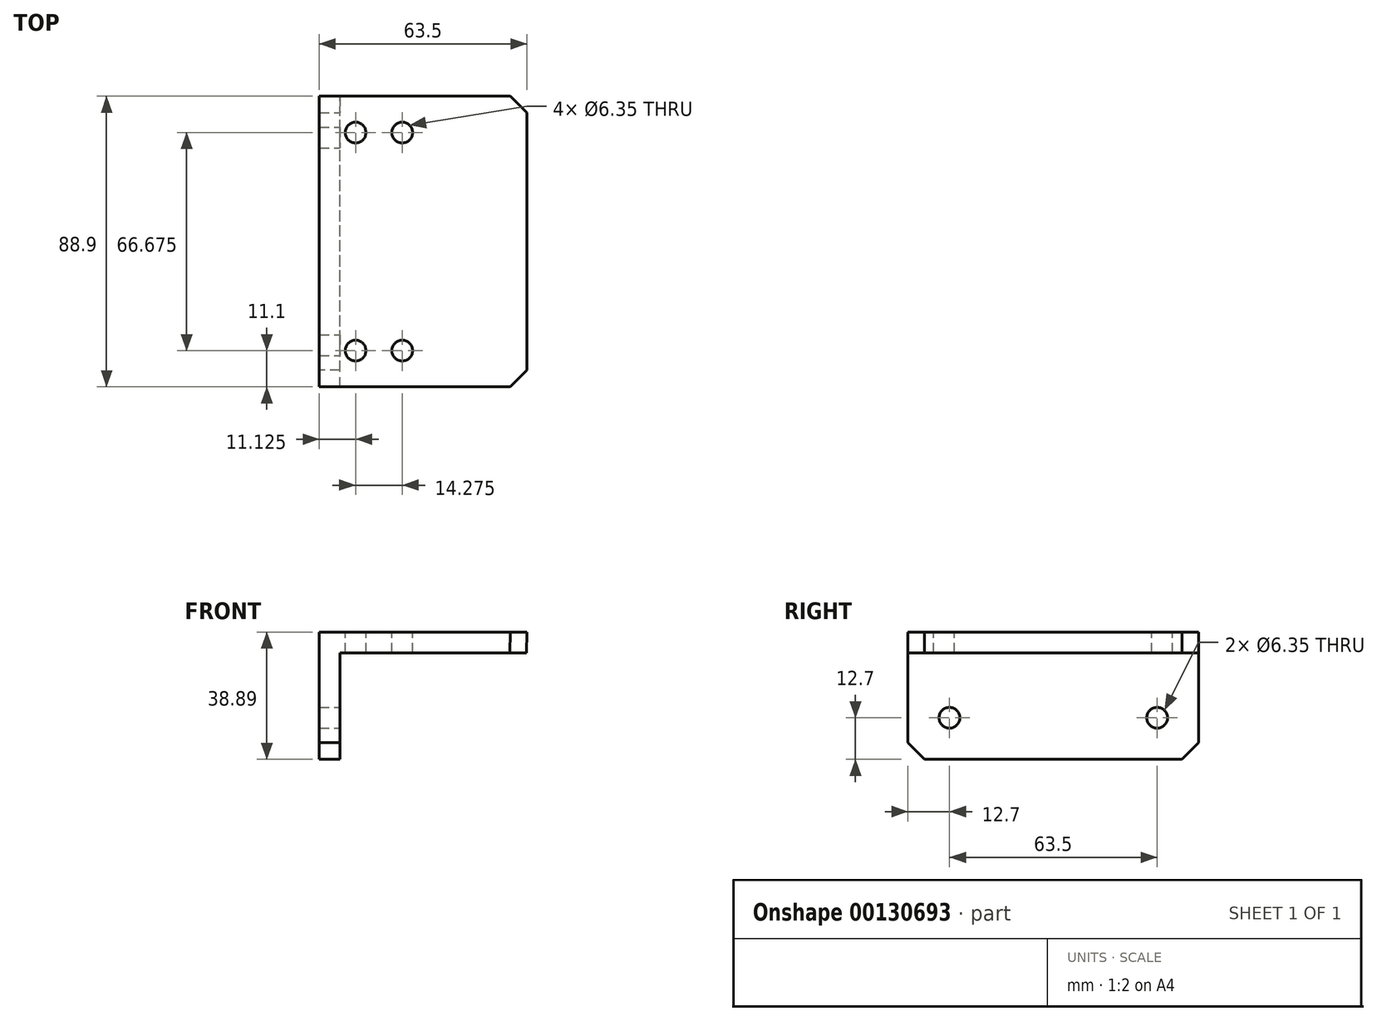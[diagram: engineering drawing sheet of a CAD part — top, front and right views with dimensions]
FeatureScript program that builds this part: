
annotation { "Feature Type Name" : "Feature", "Feature Type Description" : "" }
export const myFeature = defineFeature(function(context is Context, id is Id, definition is map)
    precondition{}
    {
        {
            var Q0;
            Q0=qCreatedBy(makeId("Front.planeOp"),FACE);
            var sketch = newSketch(context, id + "F0", { "sketchPlane" : qUnion([Q0])});
            skLineSegment(sketch, "E0", {"start": v(0, 0) * mm, "end": v(0, 38.89) * mm});
            skLineSegment(sketch, "E1", {"start": v(0, 38.89) * mm, "end": v(63.5, 38.89) * mm});
            skLineSegment(sketch, "E2", {"start": v(0, 0) * mm, "end": v(6.35, 0) * mm});
            skLineSegment(sketch, "E3", {"start": v(6.35, 0) * mm, "end": v(6.35, 32.54) * mm});
            skLineSegment(sketch, "E4", {"start": v(6.35, 32.54) * mm, "end": v(63.35, 32.54) * mm});
            skLineSegment(sketch, "E5", {"start": v(63.35, 32.54) * mm, "end": v(63.5, 38.89) * mm});
            skSolve(sketch);
        }
        {
            var Q0;
            Q0 = qSketchRegion(id + "F0", true);
            extrude(context, id + "F1", {"entities" : qUnion([Q0]), "depth" : 88.9 * mm});
        }
        {
            var Q0;
            Q0=makeQuery(id+"F1.opExtrude","SWEPT_FACE",FACE,{"disambiguationData":[OSD([sQuery(id+"F0.wireOp",EDGE,"E3")])]});
            var sketch = newSketch(context, id + "F2", { "sketchPlane" : qUnion([Q0])});
            skPoint(sketch, "E6", {"position": v(-76.2, 12.7) * mm});
            skPoint(sketch, "E7", {"position": v(-12.7, 12.7) * mm});
            skSolve(sketch);
        }
        {
            var Q0;
            Q0=sQuery(id+"F2.wireOp",VERTEX,"E6");
            var Q1;
            Q1=sQuery(id+"F2.wireOp",VERTEX,"E7");
            var Q2;
            Q2=makeQuery(id+"F1.opExtrude","SWEPT_BODY",BODY,{"disambiguationData":[OSD([sQuery(id+"F0.wireOp",EDGE,"E0"),sQuery(id+"F0.wireOp",EDGE,"E1"),sQuery(id+"F0.wireOp",EDGE,"E2"),sQuery(id+"F0.wireOp",EDGE,"E3"),sQuery(id+"F0.wireOp",EDGE,"E4"),sQuery(id+"F0.wireOp",EDGE,"E5")])]});
            hole(context, id + "F3", {"style" : HoleStyle.SIMPLE, "endStyle" : HoleEndStyle.THROUGH, "holeDiameter" : 6.35 * mm, "locations" : qUnion([Q0, Q1]), "scope" : qUnion([Q2]), "isTappedThrough" : true});
        }
        {
            var Q0;
            Q0=makeQuery(id+"F1.opExtrude","CAP_EDGE",EDGE,{"disambiguationData":[OSD([sQuery(id+"F0.wireOp",EDGE,"E5")])],"isStart":true});
            var Q1;
            Q1=makeQuery(id+"F1.opExtrude","CAP_EDGE",EDGE,{"disambiguationData":[OSD([sQuery(id+"F0.wireOp",EDGE,"E5")])],"isStart":false});
            var Q2;
            Q2=makeQuery(id+"F1.opExtrude","CAP_EDGE",EDGE,{"disambiguationData":[OSD([sQuery(id+"F0.wireOp",EDGE,"E2")])],"isStart":true});
            var Q3;
            Q3=makeQuery(id+"F1.opExtrude","CAP_EDGE",EDGE,{"disambiguationData":[OSD([sQuery(id+"F0.wireOp",EDGE,"E2")])],"isStart":false});
            chamfer(context, id + "F4", {"entities" : qUnion([Q0, Q1, Q2, Q3]), "width" : 5.08 * mm, "tangentPropagation" : true});
        }
        {
            var Q0;
            Q0=makeQuery(id+"F1.opExtrude","SWEPT_FACE",FACE,{"disambiguationData":[OSD([sQuery(id+"F0.wireOp",EDGE,"E1")])]});
            var sketch = newSketch(context, id + "F5", { "sketchPlane" : qUnion([Q0])});
            skPoint(sketch, "E8", {"position": v(11.13, -11.13) * mm});
            skPoint(sketch, "E9", {"position": v(25.4, -11.13) * mm});
            skPoint(sketch, "E10", {"position": v(11.13, -77.8) * mm});
            skPoint(sketch, "E11", {"position": v(25.4, -77.8) * mm});
            skSolve(sketch);
        }
        {
            var Q0;
            Q0=sQuery(id+"F5.wireOp",VERTEX,"E8");
            var Q1;
            Q1=sQuery(id+"F5.wireOp",VERTEX,"E9");
            var Q2;
            Q2=sQuery(id+"F5.wireOp",VERTEX,"E11");
            var Q3;
            Q3=sQuery(id+"F5.wireOp",VERTEX,"E10");
            var Q4;
            Q4=makeQuery(id+"F1.opExtrude","SWEPT_BODY",BODY,{"disambiguationData":[OSD([sQuery(id+"F0.wireOp",EDGE,"E0"),sQuery(id+"F0.wireOp",EDGE,"E1"),sQuery(id+"F0.wireOp",EDGE,"E2"),sQuery(id+"F0.wireOp",EDGE,"E3"),sQuery(id+"F0.wireOp",EDGE,"E4"),sQuery(id+"F0.wireOp",EDGE,"E5")])]});
            hole(context, id + "F6", {"style" : HoleStyle.SIMPLE, "endStyle" : HoleEndStyle.THROUGH, "holeDiameter" : 6.35 * mm, "locations" : qUnion([Q0, Q1, Q2, Q3]), "scope" : qUnion([Q4]), "isTappedThrough" : true});
        }
    });
